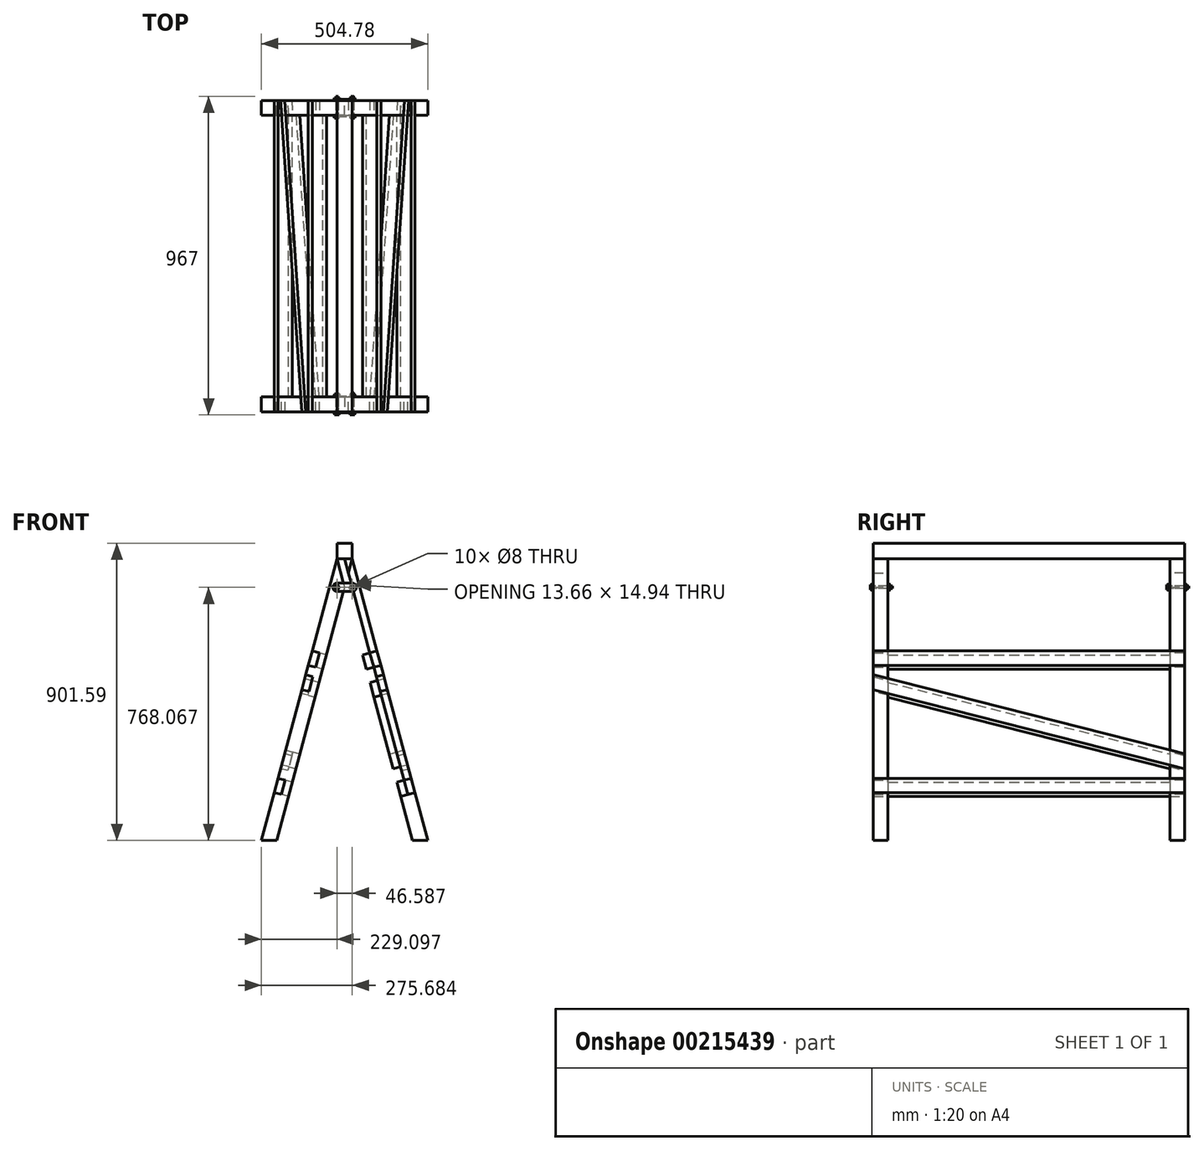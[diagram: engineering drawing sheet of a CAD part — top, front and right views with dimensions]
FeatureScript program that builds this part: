
annotation { "Feature Type Name" : "Feature", "Feature Type Description" : "" }
export const myFeature = defineFeature(function(context is Context, id is Id, definition is map)
    precondition{}
    {
        {
            var Q0;
            Q0=qCreatedBy(makeId("Front.planeOp"),FACE);
            var sketch = newSketch(context, id + "F0", { "sketchPlane" : qUnion([Q0])});
            skLineSegment(sketch, "E0", {"start": v(0, 0) * mm, "end": v(229.1, 855) * mm});
            skLineSegment(sketch, "E1", {"start": v(229.1, 855) * mm, "end": v(275.68, 855) * mm});
            skLineSegment(sketch, "E2", {"start": v(275.68, 855) * mm, "end": v(46.59, 0) * mm});
            skLineSegment(sketch, "E3", {"start": v(46.59, 0) * mm, "end": v(0, 0) * mm});
            skLineSegment(sketch, "E4", {"start": v(0, 0) * mm, "end": v(0, 446.48) * mm, "construction": true});
            skSolve(sketch);
        }
        {
            var Q0;
            Q0 = qSketchRegion(id + "F0", true);
            extrude(context, id + "F1", {"entities" : qUnion([Q0]), "depth" : 45 * mm});
        }
        {
            var Q0;
            Q0=qCreatedBy(makeId("Front.planeOp"),FACE);
            var sketch = newSketch(context, id + "F2", { "sketchPlane" : qUnion([Q0])});
            skLineSegment(sketch, "E5", {"start": v(275.68, 855) * mm, "end": v(504.78, 0) * mm});
            skLineSegment(sketch, "E6", {"start": v(504.78, 0) * mm, "end": v(458.2, 0) * mm});
            skLineSegment(sketch, "E7", {"start": v(458.2, 0) * mm, "end": v(252.4, 768.07) * mm});
            skLineSegment(sketch, "E8", {"start": v(252.4, 768.07) * mm, "end": v(275.68, 855) * mm});
            skLineSegment(sketch, "E9", {"start": v(504.78, 0) * mm, "end": v(504.78, 781.78) * mm, "construction": true});
            skSolve(sketch);
        }
        {
            var Q0;
            Q0 = qSketchRegion(id + "F2", true);
            extrude(context, id + "F3", {"entities" : qUnion([Q0]), "depth" : 45 * mm});
        }
        {
            var Q0;
            Q0=makeQuery(id+"F1.opExtrude","CAP_FACE",FACE,{"disambiguationData":[OSD([sQuery(id+"F0.wireOp",EDGE,"E0"),sQuery(id+"F0.wireOp",EDGE,"E1"),sQuery(id+"F0.wireOp",EDGE,"E2"),sQuery(id+"F0.wireOp",EDGE,"E3")])],"isStart":false});
            var sketch = newSketch(context, id + "F4", { "sketchPlane" : qUnion([Q0])});
            skLineSegment(sketch, "E10", {"start": v(93.2, 768.07) * mm, "end": v(264.17, 768.07) * mm, "construction": true});
            skLineSegment(sketch, "E11", {"start": v(222.87, 744.83) * mm, "end": v(200.8, 662.46) * mm, "construction": true});
            skLineSegment(sketch, "E12", {"start": v(273.1, 777.7) * mm, "end": v(292.14, 706.67) * mm, "construction": true});
            skCircle(sketch, "E13", {"center": v(229.1, 768.07) * mm, "radius": 4 * mm});
            skCircle(sketch, "E14", {"center": v(275.68, 768.07) * mm, "radius": 4 * mm});
            skSolve(sketch);
        }
        {
            var Q0;
            Q0 = qSketchRegion(id + "F4", true);
            extrude(context, id + "F5", {"entities" : qUnion([Q0]), "operationType" : NewBodyOperationType.REMOVE, "endBound" : BoundingType.THROUGH_ALL, "oppositeDirection" : true, "depth" : 25 * mm});
        }
        {
            var Q0;
            Q0=makeQuery(id+"F1.opExtrude","CAP_FACE",FACE,{"disambiguationData":[OSD([sQuery(id+"F0.wireOp",EDGE,"E0"),sQuery(id+"F0.wireOp",EDGE,"E1"),sQuery(id+"F0.wireOp",EDGE,"E2"),sQuery(id+"F0.wireOp",EDGE,"E3")])],"isStart":false});
            var sketch = newSketch(context, id + "F6", { "sketchPlane" : qUnion([Q0])});
            skLineSegment(sketch, "E15", {"start": v(229.1, 780.57) * mm, "end": v(275.68, 780.57) * mm});
            skLineSegment(sketch, "E16", {"start": v(229.1, 755.57) * mm, "end": v(275.68, 755.57) * mm});
            skCircle(sketch, "E17.0", {"center": v(229.1, 768.07) * mm, "radius": 4 * mm});
            skCircle(sketch, "E18.0", {"center": v(275.68, 768.07) * mm, "radius": 4 * mm});
            skLineSegment(sketch, "E19", {"start": v(229.1, 768.07) * mm, "end": v(275.68, 768.07) * mm, "construction": true});
            skArc(sketch, "E20", {"start": v(229.1, 780.57) * mm, "mid": v(216.6, 768.07) * mm, "end": v(229.1, 755.57) * mm});
            skArc(sketch, "E21", {"start": v(275.68, 780.57) * mm, "mid": v(288.18, 768.07) * mm, "end": v(275.68, 755.57) * mm});
            skSolve(sketch);
        }
        {
            var Q0;
            Q0 = qSketchRegion(id + "F6", true);
            extrude(context, id + "F7", {"entities" : qUnion([Q0]), "depth" : 3 * mm});
        }
        {
            var Q0;
            Q0=makeQuery(id+"F1.opExtrude","CAP_FACE",FACE,{"disambiguationData":[OSD([sQuery(id+"F0.wireOp",EDGE,"E0"),sQuery(id+"F0.wireOp",EDGE,"E1"),sQuery(id+"F0.wireOp",EDGE,"E2"),sQuery(id+"F0.wireOp",EDGE,"E3")])],"isStart":false});
            var Q1;
            Q1=makeQuery(id+"F1.opExtrude","CAP_FACE",FACE,{"disambiguationData":[OSD([sQuery(id+"F0.wireOp",EDGE,"E0"),sQuery(id+"F0.wireOp",EDGE,"E1"),sQuery(id+"F0.wireOp",EDGE,"E2"),sQuery(id+"F0.wireOp",EDGE,"E3")])],"isStart":true});
            cPlane(context, id + "F8", {"entities" : qUnion([Q0, Q1]), "cplaneType" : CPlaneType.MID_PLANE, "offset" : 25 * mm, "width" : 150 * mm, "height" : 150 * mm});
        }
        {
            var Q0;
            Q0=makeQuery(id+"F7.opExtrude","SWEPT_BODY",BODY,{"disambiguationData":[OSD([sQuery(id+"F6.wireOp",EDGE,"E15"),sQuery(id+"F6.wireOp",EDGE,"E16"),sQuery(id+"F6.wireOp",EDGE,"E17.0"),sQuery(id+"F6.wireOp",EDGE,"E18.0"),sQuery(id+"F6.wireOp",EDGE,"E20"),sQuery(id+"F6.wireOp",EDGE,"E21")])]});
            var Q1;
            Q1=qCreatedBy(id+"F8.planeOp",FACE);
            mirror(context, id + "F9", {"entities" : qUnion([Q0]), "mirrorPlane" : qUnion([Q1])});
        }
        {
            var Q0;
            Q0=makeQuery(id+"F7.opExtrude","CAP_FACE",FACE,{"disambiguationData":[OSD([sQuery(id+"F6.wireOp",EDGE,"E15"),sQuery(id+"F6.wireOp",EDGE,"E16"),sQuery(id+"F6.wireOp",EDGE,"E17.0"),sQuery(id+"F6.wireOp",EDGE,"E18.0"),sQuery(id+"F6.wireOp",EDGE,"E20"),sQuery(id+"F6.wireOp",EDGE,"E21")])],"isStart":false});
            var sketch = newSketch(context, id + "F10", { "sketchPlane" : qUnion([Q0])});
            skCircle(sketch, "E22.0", {"center": v(229.1, 768.07) * mm, "radius": 4 * mm});
            skCircle(sketch, "E23.0", {"center": v(275.68, 768.07) * mm, "radius": 4 * mm});
            skSolve(sketch);
        }
        {
            var Q0;
            Q0 = qSketchRegion(id + "F10", true);
            extrude(context, id + "F11", {"entities" : qUnion([Q0]), "oppositeDirection" : true, "depth" : (3 + 45 + 3 + 10) * mm});
        }
        {
            var Q0;
            Q0=makeQuery(id+"F11.opExtrude","CAP_FACE",FACE,{"disambiguationData":[OSD([sQuery(id+"F10.wireOp",EDGE,"E22.0")])],"isStart":true});
            var sketch = newSketch(context, id + "F12", { "sketchPlane" : qUnion([Q0])});
            skCircle(sketch, "E24.cCircle", {"center": v(229.1, 768.07) * mm, "radius": 6.5 * mm, "construction": true});
            skLineSegment(sketch, "E24.0", {"start": v(236.2, 765.65) * mm, "end": v(230.56, 760.7) * mm});
            skLineSegment(sketch, "E24.1", {"start": v(230.56, 760.7) * mm, "end": v(223.45, 763.12) * mm});
            skLineSegment(sketch, "E24.2", {"start": v(223.45, 763.12) * mm, "end": v(222, 770.48) * mm});
            skLineSegment(sketch, "E24.3", {"start": v(222, 770.48) * mm, "end": v(227.64, 775.43) * mm});
            skLineSegment(sketch, "E24.4", {"start": v(227.64, 775.43) * mm, "end": v(234.74, 773.01) * mm});
            skLineSegment(sketch, "E24.5", {"start": v(234.74, 773.01) * mm, "end": v(236.2, 765.65) * mm});
            skPoint(sketch, "E24.0.midPoint", {"position": v(233.38, 763.18) * mm});
            skCircle(sketch, "E25.cCircle", {"center": v(275.68, 768.07) * mm, "radius": 6.5 * mm, "construction": true});
            skLineSegment(sketch, "E25.0", {"start": v(281.8, 763.7) * mm, "end": v(274.97, 760.6) * mm});
            skLineSegment(sketch, "E25.1", {"start": v(274.97, 760.6) * mm, "end": v(268.85, 764.95) * mm});
            skLineSegment(sketch, "E25.2", {"start": v(268.85, 764.95) * mm, "end": v(269.57, 772.42) * mm});
            skLineSegment(sketch, "E25.3", {"start": v(269.57, 772.42) * mm, "end": v(276.4, 775.54) * mm});
            skLineSegment(sketch, "E25.4", {"start": v(276.4, 775.54) * mm, "end": v(282.51, 771.18) * mm});
            skLineSegment(sketch, "E25.5", {"start": v(282.51, 771.18) * mm, "end": v(281.8, 763.7) * mm});
            skPoint(sketch, "E25.0.midPoint", {"position": v(278.38, 762.15) * mm});
            skSolve(sketch);
        }
        {
            var Q0;
            Q0 = qSketchRegion(id + "F12", true);
            extrude(context, id + "F13", {"entities" : qUnion([Q0]), "operationType" : NewBodyOperationType.ADD, "depth" : 6 * mm});
        }
        {
            var Q0;
            Q0=makeQuery(id+"F9.opPattern","COPY",FACE,{"derivedFrom":makeQuery(id+"F7.opExtrude","CAP_FACE",FACE,{"disambiguationData":[OSD([sQuery(id+"F6.wireOp",EDGE,"E15"),sQuery(id+"F6.wireOp",EDGE,"E16"),sQuery(id+"F6.wireOp",EDGE,"E17.0"),sQuery(id+"F6.wireOp",EDGE,"E18.0"),sQuery(id+"F6.wireOp",EDGE,"E20"),sQuery(id+"F6.wireOp",EDGE,"E21")])],"isStart":false}),"instanceName":"1"});
            var sketch = newSketch(context, id + "F14", { "sketchPlane" : qUnion([Q0])});
            skCircle(sketch, "E26.0", {"center": v(-275.68, 768.07) * mm, "radius": 4 * mm});
            skCircle(sketch, "E27.0.0", {"center": v(-229.1, 768.07) * mm, "radius": 4 * mm});
            skCircle(sketch, "E28.cCircle", {"center": v(-275.68, 768.07) * mm, "radius": 6.5 * mm, "construction": true});
            skLineSegment(sketch, "E28.0", {"start": v(-268.19, 768.45) * mm, "end": v(-271.6, 761.77) * mm});
            skLineSegment(sketch, "E28.1", {"start": v(-271.6, 761.77) * mm, "end": v(-279.1, 761.38) * mm});
            skLineSegment(sketch, "E28.2", {"start": v(-279.1, 761.38) * mm, "end": v(-283.18, 767.68) * mm});
            skLineSegment(sketch, "E28.3", {"start": v(-283.18, 767.68) * mm, "end": v(-279.77, 774.36) * mm});
            skLineSegment(sketch, "E28.4", {"start": v(-279.77, 774.36) * mm, "end": v(-272.27, 774.75) * mm});
            skLineSegment(sketch, "E28.5", {"start": v(-272.27, 774.75) * mm, "end": v(-268.19, 768.45) * mm});
            skPoint(sketch, "E28.0.midPoint", {"position": v(-269.9, 765.11) * mm});
            skCircle(sketch, "E29.cCircle", {"center": v(-229.1, 768.07) * mm, "radius": 6.5 * mm, "construction": true});
            skLineSegment(sketch, "E29.0", {"start": v(-225.02, 774.37) * mm, "end": v(-221.6, 767.68) * mm});
            skLineSegment(sketch, "E29.1", {"start": v(-221.6, 767.68) * mm, "end": v(-225.68, 761.38) * mm});
            skLineSegment(sketch, "E29.2", {"start": v(-225.68, 761.38) * mm, "end": v(-233.18, 761.77) * mm});
            skLineSegment(sketch, "E29.3", {"start": v(-233.18, 761.77) * mm, "end": v(-236.6, 768.45) * mm});
            skLineSegment(sketch, "E29.4", {"start": v(-236.6, 768.45) * mm, "end": v(-232.51, 774.75) * mm});
            skLineSegment(sketch, "E29.5", {"start": v(-232.51, 774.75) * mm, "end": v(-225.02, 774.37) * mm});
            skPoint(sketch, "E29.0.midPoint", {"position": v(-223.3, 771.03) * mm});
            skSolve(sketch);
        }
        {
            var Q0;
            Q0 = qSketchRegion(id + "F14", true);
            extrude(context, id + "F15", {"entities" : qUnion([Q0]), "depth" : 6 * mm});
        }
        {
            var Q0;
            Q0=makeQuery(id+"F9.opPattern","COPY",BODY,{"derivedFrom":makeQuery(id+"F7.opExtrude","SWEPT_BODY",BODY,{"disambiguationData":[OSD([sQuery(id+"F6.wireOp",EDGE,"E15"),sQuery(id+"F6.wireOp",EDGE,"E16"),sQuery(id+"F6.wireOp",EDGE,"E17.0"),sQuery(id+"F6.wireOp",EDGE,"E18.0"),sQuery(id+"F6.wireOp",EDGE,"E20"),sQuery(id+"F6.wireOp",EDGE,"E21")])]}),"instanceName":"1"});
            var Q1;
            Q1=makeQuery(id+"F3.opExtrude","SWEPT_BODY",BODY,{"disambiguationData":[OSD([sQuery(id+"F2.wireOp",EDGE,"E5"),sQuery(id+"F2.wireOp",EDGE,"E6"),sQuery(id+"F2.wireOp",EDGE,"E7"),sQuery(id+"F2.wireOp",EDGE,"E8")])]});
            var Q2;
            Q2=makeQuery(id+"F1.opExtrude","SWEPT_BODY",BODY,{"disambiguationData":[OSD([sQuery(id+"F0.wireOp",EDGE,"E0"),sQuery(id+"F0.wireOp",EDGE,"E1"),sQuery(id+"F0.wireOp",EDGE,"E2"),sQuery(id+"F0.wireOp",EDGE,"E3")])]});
            var Q3;
            Q3=makeQuery(id+"F11.opExtrude","SWEPT_BODY",BODY,{"disambiguationData":[OSD([sQuery(id+"F10.wireOp",EDGE,"E23.0")])]});
            var Q4;
            Q4=makeQuery(id+"F11.opExtrude","SWEPT_BODY",BODY,{"disambiguationData":[OSD([sQuery(id+"F10.wireOp",EDGE,"E22.0")])]});
            var Q5;
            Q5=makeQuery(id+"F15.opExtrude","SWEPT_BODY",BODY,{"disambiguationData":[OSD([sQuery(id+"F14.wireOp",EDGE,"E27.0.0"),sQuery(id+"F14.wireOp",EDGE,"E29.0"),sQuery(id+"F14.wireOp",EDGE,"E29.1"),sQuery(id+"F14.wireOp",EDGE,"E29.2"),sQuery(id+"F14.wireOp",EDGE,"E29.3"),sQuery(id+"F14.wireOp",EDGE,"E29.4"),sQuery(id+"F14.wireOp",EDGE,"E29.5")])]});
            var Q6;
            Q6=makeQuery(id+"F15.opExtrude","SWEPT_BODY",BODY,{"disambiguationData":[OSD([sQuery(id+"F14.wireOp",EDGE,"E26.0"),sQuery(id+"F14.wireOp",EDGE,"E28.0"),sQuery(id+"F14.wireOp",EDGE,"E28.1"),sQuery(id+"F14.wireOp",EDGE,"E28.2"),sQuery(id+"F14.wireOp",EDGE,"E28.3"),sQuery(id+"F14.wireOp",EDGE,"E28.4"),sQuery(id+"F14.wireOp",EDGE,"E28.5")])]});
            var Q7;
            Q7=makeQuery(id+"F7.opExtrude","SWEPT_BODY",BODY,{"disambiguationData":[OSD([sQuery(id+"F6.wireOp",EDGE,"E15"),sQuery(id+"F6.wireOp",EDGE,"E16"),sQuery(id+"F6.wireOp",EDGE,"E17.0"),sQuery(id+"F6.wireOp",EDGE,"E18.0"),sQuery(id+"F6.wireOp",EDGE,"E20"),sQuery(id+"F6.wireOp",EDGE,"E21")])]});
            var Q8;
            Q8=makeQuery(id+"F3.opExtrude","SWEPT_EDGE",EDGE,{"disambiguationData":[OSD([sQuery(id+"F2.wireOp",EDGE,"E5"),sQuery(id+"F2.wireOp",EDGE,"E6")])]});
            transform(context, id + "F16", {"entities" : qUnion([Q0, Q1, Q2, Q3, Q4, Q5, Q6, Q7]), "transformType" : TransformType.TRANSLATION_DISTANCE, "transformDirection" : qUnion([Q8]), "distance" : 900 * mm, "makeCopy" : true});
        }
        {
            var Q0;
            Q0=makeQuery(id+"F3.opExtrude","SWEPT_FACE",FACE,{"disambiguationData":[OSD([sQuery(id+"F2.wireOp",EDGE,"E5")])]});
            var sketch = newSketch(context, id + "F17", { "sketchPlane" : qUnion([Q0])});
            skLineSegment(sketch, "E30.bottom", {"start": v(-45, 64.35) * mm, "end": v(900, 64.35) * mm});
            skLineSegment(sketch, "E30.top", {"start": v(-45, 19.35) * mm, "end": v(900, 19.35) * mm});
            skLineSegment(sketch, "E30.left", {"start": v(-45, 64.35) * mm, "end": v(-45, 19.35) * mm});
            skLineSegment(sketch, "E30.right", {"start": v(900, 64.35) * mm, "end": v(900, 19.35) * mm});
            skLineSegment(sketch, "E31.bottom", {"start": v(-45, 464.35) * mm, "end": v(900, 464.35) * mm});
            skLineSegment(sketch, "E31.top", {"start": v(-45, 419.35) * mm, "end": v(900, 419.35) * mm});
            skLineSegment(sketch, "E31.left", {"start": v(-45, 464.35) * mm, "end": v(-45, 419.35) * mm});
            skLineSegment(sketch, "E31.right", {"start": v(900, 464.35) * mm, "end": v(900, 419.35) * mm});
            skSolve(sketch);
        }
        {
            var Q0;
            Q0 = qSketchRegion(id + "F17", true);
            extrude(context, id + "F18", {"entities" : qUnion([Q0]), "oppositeDirection" : true, "depth" : 45 * mm});
        }
        {
            var Q0;
            {var subQ3=sQuery(id+"F2.wireOp",EDGE,"E5");Q0=makeQuery(id+"F23.opBoolean","SPLIT",FACE,{"disambiguationData":[TD([makeQuery(id+"F18.opExtrude","SWEPT_FACE",FACE,{"disambiguationData":[OSD([sQuery(id+"F17.wireOp",EDGE,"E30.bottom")])]})])],"derivedFrom":makeQuery(id+"F3.opExtrude","SWEPT_FACE",FACE,{"disambiguationData":[OSD([subQ3])]})});}
            var sketch = newSketch(context, id + "F19", { "sketchPlane" : qUnion([Q0])});
            skLineSegment(sketch, "E32", {"start": v(-45, 389.35) * mm, "end": v(900, 140.88) * mm});
            skLineSegment(sketch, "E33", {"start": v(900, 140.88) * mm, "end": v(900, 94.35) * mm});
            skLineSegment(sketch, "E34", {"start": v(900, 94.35) * mm, "end": v(-45, 342.82) * mm});
            skLineSegment(sketch, "E35", {"start": v(-45, 342.82) * mm, "end": v(-45, 389.35) * mm});
            skSolve(sketch);
        }
        {
            var Q0;
            Q0 = qSketchRegion(id + "F19", true);
            extrude(context, id + "F20", {"entities" : qUnion([Q0]), "oppositeDirection" : true, "depth" : 45 * mm});
        }
        {
            var Q0;
            Q0=makeQuery(id+"F18.opExtrude","SWEPT_FACE",FACE,{"disambiguationData":[OSD([sQuery(id+"F17.wireOp",EDGE,"E30.top")])]});
            var sketch = newSketch(context, id + "F21", { "sketchPlane" : qUnion([Q0])});
            skLineSegment(sketch, "E36.bottom", {"start": v(442.58, 45) * mm, "end": v(465.08, 45) * mm});
            skLineSegment(sketch, "E36.top", {"start": v(442.58, 0) * mm, "end": v(465.08, 0) * mm});
            skLineSegment(sketch, "E36.left", {"start": v(442.58, 45) * mm, "end": v(442.58, 0) * mm});
            skLineSegment(sketch, "E36.right", {"start": v(465.08, 45) * mm, "end": v(465.08, 0) * mm});
            skLineSegment(sketch, "E37.bottom", {"start": v(442.58, -900) * mm, "end": v(465.08, -900) * mm});
            skLineSegment(sketch, "E37.top", {"start": v(442.58, -855) * mm, "end": v(465.08, -855) * mm});
            skLineSegment(sketch, "E37.left", {"start": v(442.58, -900) * mm, "end": v(442.58, -855) * mm});
            skLineSegment(sketch, "E37.right", {"start": v(465.08, -900) * mm, "end": v(465.08, -855) * mm});
            skSolve(sketch);
        }
        {
            var Q0;
            Q0 = qSketchRegion(id + "F21", true);
            extrude(context, id + "F22", {"entities" : qUnion([Q0]), "operationType" : NewBodyOperationType.REMOVE, "endBound" : BoundingType.THROUGH_ALL, "oppositeDirection" : true, "depth" : 25 * mm});
        }
        {
            var Q0;
            Q0=makeQuery(id+"F18.opExtrude","SWEPT_BODY",BODY,{"disambiguationData":[OSD([sQuery(id+"F17.wireOp",EDGE,"E31.bottom"),sQuery(id+"F17.wireOp",EDGE,"E31.top"),sQuery(id+"F17.wireOp",EDGE,"E31.left"),sQuery(id+"F17.wireOp",EDGE,"E31.right")])]});
            var Q1;
            Q1=makeQuery(id+"F18.opExtrude","SWEPT_BODY",BODY,{"disambiguationData":[OSD([sQuery(id+"F17.wireOp",EDGE,"E30.bottom"),sQuery(id+"F17.wireOp",EDGE,"E30.top"),sQuery(id+"F17.wireOp",EDGE,"E30.left"),sQuery(id+"F17.wireOp",EDGE,"E30.right")])]});
            var Q2;
            Q2=makeQuery(id+"F20.opExtrude","SWEPT_BODY",BODY,{"disambiguationData":[OSD([sQuery(id+"F19.wireOp",EDGE,"E32"),sQuery(id+"F19.wireOp",EDGE,"E33"),sQuery(id+"F19.wireOp",EDGE,"E34"),sQuery(id+"F19.wireOp",EDGE,"E35")])]});
            var Q3;
            Q3=makeQuery(id+"F3.opExtrude","SWEPT_BODY",BODY,{"disambiguationData":[OSD([sQuery(id+"F2.wireOp",EDGE,"E5"),sQuery(id+"F2.wireOp",EDGE,"E6"),sQuery(id+"F2.wireOp",EDGE,"E7"),sQuery(id+"F2.wireOp",EDGE,"E8")])]});
            var Q4;
            Q4=makeQuery(id+"F16.opPattern","COPY",BODY,{"derivedFrom":makeQuery(id+"F3.opExtrude","SWEPT_BODY",BODY,{"disambiguationData":[OSD([sQuery(id+"F2.wireOp",EDGE,"E5"),sQuery(id+"F2.wireOp",EDGE,"E6"),sQuery(id+"F2.wireOp",EDGE,"E7"),sQuery(id+"F2.wireOp",EDGE,"E8")])]}),"instanceName":"1"});
            booleanBodies(context, id + "F23", {"operationType" : BooleanOperationType.SUBTRACTION, "tools" : qUnion([Q0, Q1, Q2]), "targets" : qUnion([Q3, Q4]), "keepTools" : true});
        }
        {
            var Q0;
            {var subQ0=sQuery(id+"F2.wireOp",EDGE,"E8");var subQ3=sQuery(id+"F2.wireOp",EDGE,"E5");Q0=makeQuery(id+"F23.opBoolean","SPLIT",FACE,{"disambiguationData":[TD([makeQuery(id+"F3.opExtrude","SWEPT_FACE",FACE,{"disambiguationData":[OSD([subQ0])]})])],"derivedFrom":makeQuery(id+"F3.opExtrude","SWEPT_FACE",FACE,{"disambiguationData":[OSD([subQ3])]})});}
            var Q1;
            Q1=makeQuery(id+"F1.opExtrude","SWEPT_FACE",FACE,{"disambiguationData":[OSD([sQuery(id+"F0.wireOp",EDGE,"E0")])]});
            cPlane(context, id + "F24", {"entities" : qUnion([Q0, Q1]), "cplaneType" : CPlaneType.MID_PLANE, "offset" : 25 * mm, "width" : 150 * mm, "height" : 150 * mm});
        }
        {
            var Q0;
            Q0=makeQuery(id+"F18.opExtrude","SWEPT_BODY",BODY,{"disambiguationData":[OSD([sQuery(id+"F17.wireOp",EDGE,"E31.bottom"),sQuery(id+"F17.wireOp",EDGE,"E31.top"),sQuery(id+"F17.wireOp",EDGE,"E31.left"),sQuery(id+"F17.wireOp",EDGE,"E31.right")])]});
            var Q1;
            Q1=makeQuery(id+"F20.opExtrude","SWEPT_BODY",BODY,{"disambiguationData":[OSD([sQuery(id+"F19.wireOp",EDGE,"E32"),sQuery(id+"F19.wireOp",EDGE,"E33"),sQuery(id+"F19.wireOp",EDGE,"E34"),sQuery(id+"F19.wireOp",EDGE,"E35")])]});
            var Q2;
            Q2=makeQuery(id+"F18.opExtrude","SWEPT_BODY",BODY,{"disambiguationData":[OSD([sQuery(id+"F17.wireOp",EDGE,"E30.bottom"),sQuery(id+"F17.wireOp",EDGE,"E30.top"),sQuery(id+"F17.wireOp",EDGE,"E30.left"),sQuery(id+"F17.wireOp",EDGE,"E30.right")])]});
            var Q3;
            Q3=qCreatedBy(id+"F24.planeOp",FACE);
            mirror(context, id + "F25", {"entities" : qUnion([Q0, Q1, Q2]), "mirrorPlane" : qUnion([Q3])});
        }
        {
            var Q0;
            Q0=makeQuery(id+"F25.opPattern","COPY",BODY,{"derivedFrom":makeQuery(id+"F18.opExtrude","SWEPT_BODY",BODY,{"disambiguationData":[OSD([sQuery(id+"F17.wireOp",EDGE,"E31.bottom"),sQuery(id+"F17.wireOp",EDGE,"E31.top"),sQuery(id+"F17.wireOp",EDGE,"E31.left"),sQuery(id+"F17.wireOp",EDGE,"E31.right")])]}),"instanceName":"1"});
            var Q1;
            Q1=makeQuery(id+"F25.opPattern","COPY",BODY,{"derivedFrom":makeQuery(id+"F20.opExtrude","SWEPT_BODY",BODY,{"disambiguationData":[OSD([sQuery(id+"F19.wireOp",EDGE,"E32"),sQuery(id+"F19.wireOp",EDGE,"E33"),sQuery(id+"F19.wireOp",EDGE,"E34"),sQuery(id+"F19.wireOp",EDGE,"E35")])]}),"instanceName":"1"});
            var Q2;
            Q2=makeQuery(id+"F25.opPattern","COPY",BODY,{"derivedFrom":makeQuery(id+"F18.opExtrude","SWEPT_BODY",BODY,{"disambiguationData":[OSD([sQuery(id+"F17.wireOp",EDGE,"E30.bottom"),sQuery(id+"F17.wireOp",EDGE,"E30.top"),sQuery(id+"F17.wireOp",EDGE,"E30.left"),sQuery(id+"F17.wireOp",EDGE,"E30.right")])]}),"instanceName":"1"});
            var Q3;
            Q3=makeQuery(id+"F16.opPattern","COPY",BODY,{"derivedFrom":makeQuery(id+"F1.opExtrude","SWEPT_BODY",BODY,{"disambiguationData":[OSD([sQuery(id+"F0.wireOp",EDGE,"E0"),sQuery(id+"F0.wireOp",EDGE,"E1"),sQuery(id+"F0.wireOp",EDGE,"E2"),sQuery(id+"F0.wireOp",EDGE,"E3")])]}),"instanceName":"1"});
            var Q4;
            Q4=makeQuery(id+"F1.opExtrude","SWEPT_BODY",BODY,{"disambiguationData":[OSD([sQuery(id+"F0.wireOp",EDGE,"E0"),sQuery(id+"F0.wireOp",EDGE,"E1"),sQuery(id+"F0.wireOp",EDGE,"E2"),sQuery(id+"F0.wireOp",EDGE,"E3")])]});
            booleanBodies(context, id + "F26", {"operationType" : BooleanOperationType.SUBTRACTION, "tools" : qUnion([Q0, Q1, Q2]), "targets" : qUnion([Q3, Q4]), "keepTools" : true});
        }
        {
            var Q0;
            Q0=makeQuery(id+"F1.opExtrude","CAP_FACE",FACE,{"disambiguationData":[OSD([sQuery(id+"F0.wireOp",EDGE,"E0"),sQuery(id+"F0.wireOp",EDGE,"E1"),sQuery(id+"F0.wireOp",EDGE,"E2"),sQuery(id+"F0.wireOp",EDGE,"E3")])],"isStart":false});
            var sketch = newSketch(context, id + "F27", { "sketchPlane" : qUnion([Q0])});
            skLineSegment(sketch, "E38.bottom", {"start": v(229.1, 855) * mm, "end": v(275.68, 855) * mm});
            skLineSegment(sketch, "E38.top", {"start": v(229.1, 901.59) * mm, "end": v(275.68, 901.59) * mm});
            skLineSegment(sketch, "E38.left", {"start": v(229.1, 855) * mm, "end": v(229.1, 901.59) * mm});
            skLineSegment(sketch, "E38.right", {"start": v(275.68, 855) * mm, "end": v(275.68, 901.59) * mm});
            skSolve(sketch);
        }
        {
            var Q0;
            Q0 = qSketchRegion(id + "F27", true);
            var Q1;
            Q1=makeQuery(id+"F16.opPattern","COPY",FACE,{"derivedFrom":makeQuery(id+"F1.opExtrude","CAP_FACE",FACE,{"disambiguationData":[OSD([sQuery(id+"F0.wireOp",EDGE,"E0"),sQuery(id+"F0.wireOp",EDGE,"E1"),sQuery(id+"F0.wireOp",EDGE,"E2"),sQuery(id+"F0.wireOp",EDGE,"E3")])],"isStart":true}),"instanceName":"1"});
            extrude(context, id + "F28", {"entities" : qUnion([Q0]), "endBound" : BoundingType.UP_TO_SURFACE, "oppositeDirection" : true, "endBoundEntityFace" : qUnion([Q1]), "depth" : 25 * mm});
        }
    });
